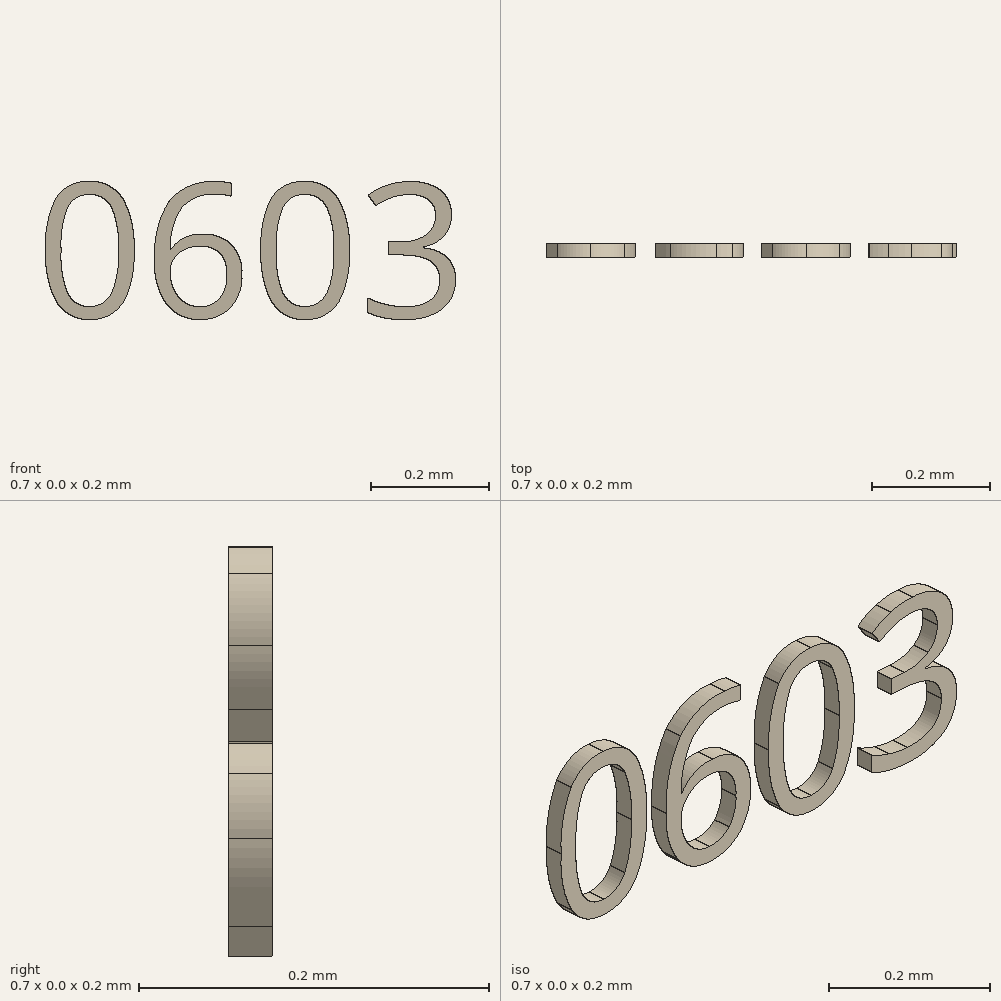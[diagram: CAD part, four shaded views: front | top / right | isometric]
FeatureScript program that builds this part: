
annotation { "Feature Type Name" : "Feature", "Feature Type Description" : "" }
export const myFeature = defineFeature(function(context is Context, id is Id, definition is map)
    precondition{}
    {
        {
            var Q0;
            Q0=qCreatedBy(makeId("Front.planeOp"),FACE);
            var sketch = newSketch(context, id + "F0", { "sketchPlane" : qUnion([Q0])});
            skText(sketch, "E0", { "text": "0603", "fontName": "OpenSans-Regular.ttf"});
            const initialGuessF0  = {"E0": [-0.00032, 8e-05, 1, 0, 0.00023]};
            skSetInitialGuess(sketch, initialGuessF0);
            skSolve(sketch);
        }
        {
            var Q0;
            Q0 = qSketchRegion(id + "F0", true);
            extrude(context, id + "F1", {"entities" : qUnion([Q0]), "depth" : 0.03 * mm});
        }
    });
